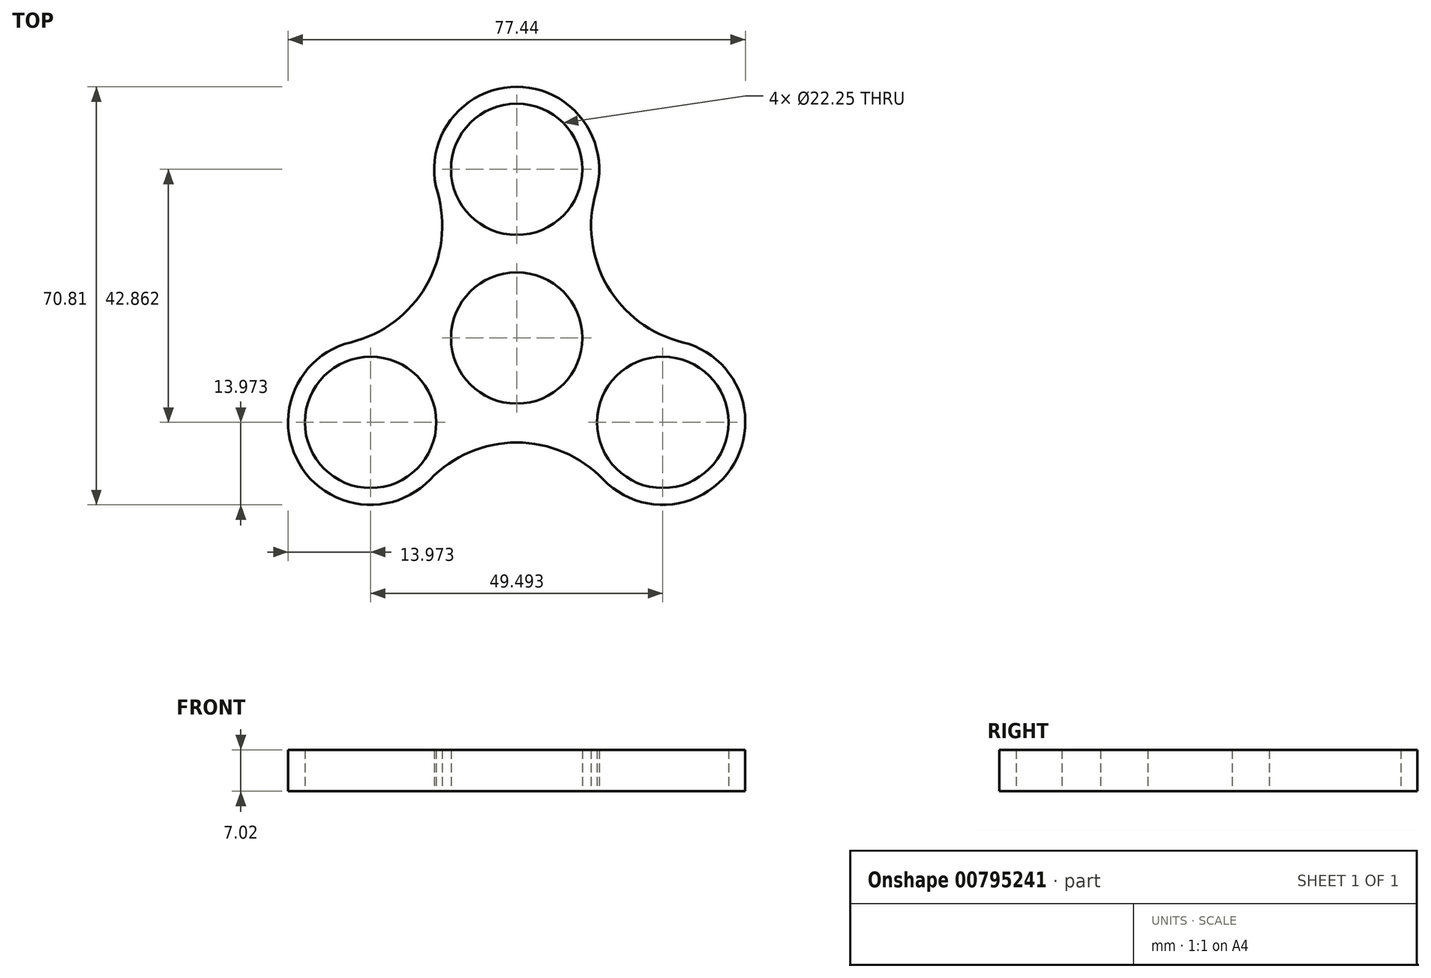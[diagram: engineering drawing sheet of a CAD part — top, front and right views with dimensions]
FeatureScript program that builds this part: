
annotation { "Feature Type Name" : "Feature", "Feature Type Description" : "" }
export const myFeature = defineFeature(function(context is Context, id is Id, definition is map)
    precondition{}
    {
        {
            var Q0;
            Q0=qCreatedBy(makeId("Top.planeOp"),FACE);
            var sketch = newSketch(context, id + "F0", { "sketchPlane" : qUnion([Q0])});
            skCircle(sketch, "E0", {"center": v(0, 0) * mm, "radius": 28.58 * mm});
            skCircle(sketch, "E1", {"center": v(0, 28.58) * mm, "radius": 13.97 * mm});
            skCircle(sketch, "E2", {"center": v(-24.75, -14.29) * mm, "radius": 13.97 * mm});
            skCircle(sketch, "E3", {"center": v(24.75, -14.29) * mm, "radius": 13.97 * mm});
            skLineSegment(sketch, "E4", {"start": v(0, 0) * mm, "end": v(-24.75, -14.29) * mm});
            skLineSegment(sketch, "E5", {"start": v(0, 0) * mm, "end": v(24.75, -14.29) * mm});
            skArc(sketch, "E6", {"start": v(14.66, -23.96) * mm, "mid": v(0, -17.7) * mm, "end": v(-14.66, -23.96) * mm});
            skArc(sketch, "E7", {"start": v(-28.08, -0.72) * mm, "mid": v(-15.33, 8.85) * mm, "end": v(-13.42, 24.68) * mm});
            skArc(sketch, "E8", {"start": v(13.42, 24.68) * mm, "mid": v(15.33, 8.85) * mm, "end": v(28.08, -0.72) * mm});
            skCircle(sketch, "E9", {"center": v(0, 0) * mm, "radius": 11.13 * mm});
            skCircle(sketch, "E10", {"center": v(0, 28.58) * mm, "radius": 11.13 * mm});
            skCircle(sketch, "E11", {"center": v(-24.75, -14.29) * mm, "radius": 11.13 * mm});
            skCircle(sketch, "E12", {"center": v(24.75, -14.29) * mm, "radius": 11.13 * mm});
            skSolve(sketch);
        }
        {
            var Q0;
            {var subQ0=sQuery(id+"F0.wireOp",EDGE,"E1");var subQ1=sQuery(id+"F0.wireOp",EDGE,"E0");var subQ2=makeQuery(id+"F0.imprint","INTERSECT",VERTEX,{"disambiguationData":[OD(0.0)],"derivedFrom":[subQ1,subQ0]});Q0=makeQuery(id+"F0.imprint","IMPRINT",FACE,{"disambiguationData":[TD([[makeQuery(id+"F0.imprint","IMPRINT",EDGE,{"disambiguationData":[TD([[subQ2,-1.0]])],"derivedFrom":subQ1}),-1.0]])]});}
            var Q1;
            {var subQ0=sQuery(id+"F0.wireOp",EDGE,"E1");var subQ2=sQuery(id+"F0.wireOp",EDGE,"E0");var subQ7=makeQuery(id+"F0.imprint","INTERSECT",VERTEX,{"disambiguationData":[OD(0.0)],"derivedFrom":[subQ2,subQ0]});Q1=makeQuery(id+"F0.imprint","IMPRINT",FACE,{"disambiguationData":[TD([[makeQuery(id+"F0.imprint","IMPRINT",EDGE,{"disambiguationData":[TD([[subQ7,-1.0]])],"derivedFrom":subQ2}),1.0]])]});}
            var Q2;
            {var subQ5=sQuery(id+"F0.wireOp",EDGE,"E7");Q2=makeQuery(id+"F0.imprint","IMPRINT",FACE,{"disambiguationData":[TD([[makeQuery(id+"F0.imprint","IMPRINT",EDGE,{"derivedFrom":subQ5}),-1.0]])]});}
            var Q3;
            {var subQ1=sQuery(id+"F0.wireOp",EDGE,"E3");var subQ6=sQuery(id+"F0.wireOp",EDGE,"E0");var subQ7=makeQuery(id+"F0.imprint","INTERSECT",VERTEX,{"disambiguationData":[OD(1.0)],"derivedFrom":[subQ6,subQ1]});Q3=makeQuery(id+"F0.imprint","IMPRINT",FACE,{"disambiguationData":[TD([[makeQuery(id+"F0.imprint","IMPRINT",EDGE,{"disambiguationData":[TD([[subQ7,1.0]])],"derivedFrom":subQ6}),1.0]])]});}
            var Q4;
            {var subQ0=sQuery(id+"F0.wireOp",EDGE,"E3");var subQ1=sQuery(id+"F0.wireOp",EDGE,"E0");var subQ2=makeQuery(id+"F0.imprint","INTERSECT",VERTEX,{"disambiguationData":[OD(0.0)],"derivedFrom":[subQ1,subQ0]});Q4=makeQuery(id+"F0.imprint","IMPRINT",FACE,{"disambiguationData":[TD([[makeQuery(id+"F0.imprint","IMPRINT",EDGE,{"disambiguationData":[TD([[subQ2,-1.0]])],"derivedFrom":subQ1}),-1.0]])]});}
            var Q5;
            {var subQ0=sQuery(id+"F0.wireOp",EDGE,"E3");var subQ2=sQuery(id+"F0.wireOp",EDGE,"E0");var subQ3=makeQuery(id+"F0.imprint","INTERSECT",VERTEX,{"disambiguationData":[OD(0.0)],"derivedFrom":[subQ2,subQ0]});Q5=makeQuery(id+"F0.imprint","IMPRINT",FACE,{"disambiguationData":[TD([[makeQuery(id+"F0.imprint","IMPRINT",EDGE,{"disambiguationData":[TD([[subQ3,-1.0]])],"derivedFrom":subQ2}),1.0]])]});}
            var Q6;
            {var subQ5=sQuery(id+"F0.wireOp",EDGE,"E6");Q6=makeQuery(id+"F0.imprint","IMPRINT",FACE,{"disambiguationData":[TD([[makeQuery(id+"F0.imprint","IMPRINT",EDGE,{"derivedFrom":subQ5}),-1.0]])]});}
            var Q7;
            {var subQ1=sQuery(id+"F0.wireOp",EDGE,"E2");var subQ6=sQuery(id+"F0.wireOp",EDGE,"E0");var subQ7=makeQuery(id+"F0.imprint","INTERSECT",VERTEX,{"disambiguationData":[OD(1.0)],"derivedFrom":[subQ6,subQ1]});Q7=makeQuery(id+"F0.imprint","IMPRINT",FACE,{"disambiguationData":[TD([[makeQuery(id+"F0.imprint","IMPRINT",EDGE,{"disambiguationData":[TD([[subQ7,1.0]])],"derivedFrom":subQ6}),1.0]])]});}
            var Q8;
            {var subQ1=sQuery(id+"F0.wireOp",EDGE,"E2");var subQ6=sQuery(id+"F0.wireOp",EDGE,"E0");var subQ7=makeQuery(id+"F0.imprint","INTERSECT",VERTEX,{"disambiguationData":[OD(0.0)],"derivedFrom":[subQ6,subQ1]});Q8=makeQuery(id+"F0.imprint","IMPRINT",FACE,{"disambiguationData":[TD([[makeQuery(id+"F0.imprint","IMPRINT",EDGE,{"disambiguationData":[TD([[subQ7,-1.0]])],"derivedFrom":subQ6}),1.0]])]});}
            var Q9;
            {var subQ0=sQuery(id+"F0.wireOp",EDGE,"E2");var subQ1=sQuery(id+"F0.wireOp",EDGE,"E0");var subQ2=makeQuery(id+"F0.imprint","INTERSECT",VERTEX,{"disambiguationData":[OD(0.0)],"derivedFrom":[subQ1,subQ0]});Q9=makeQuery(id+"F0.imprint","IMPRINT",FACE,{"disambiguationData":[TD([[makeQuery(id+"F0.imprint","IMPRINT",EDGE,{"disambiguationData":[TD([[subQ2,-1.0]])],"derivedFrom":subQ1}),-1.0]])]});}
            extrude(context, id + "F1", {"entities" : qUnion([Q0, Q1, Q2, Q3, Q4, Q5, Q6, Q7, Q8, Q9]), "endBound" : BoundingType.SYMMETRIC, "depth" : 7 * mm, "offsetDistance" : 25.4 * mm});
        }
    });
